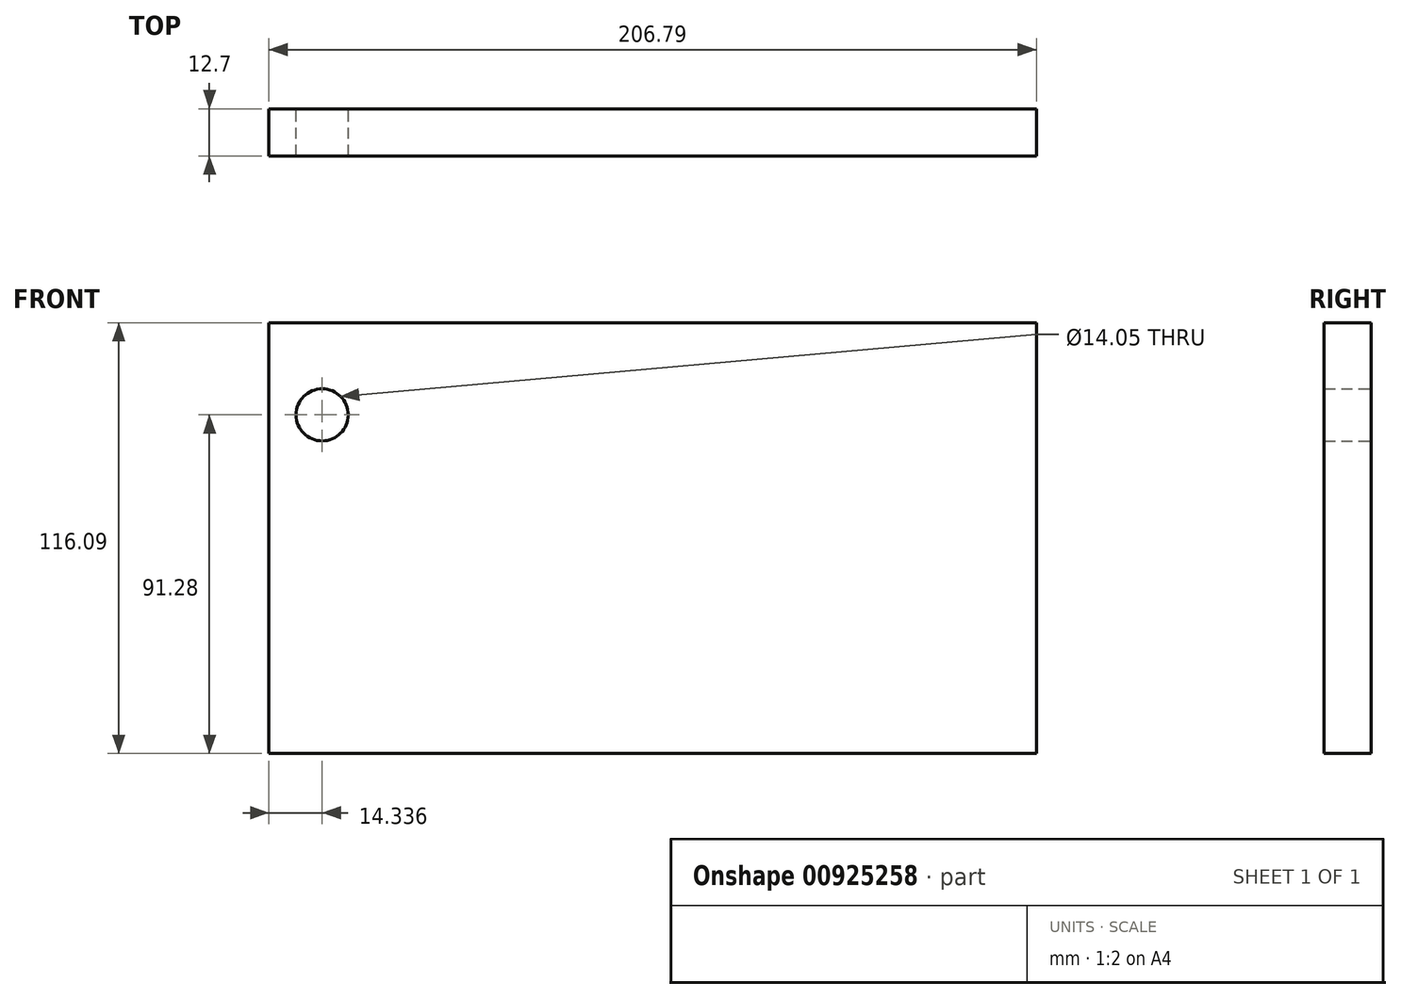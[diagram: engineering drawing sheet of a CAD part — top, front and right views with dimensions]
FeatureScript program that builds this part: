
annotation { "Feature Type Name" : "Feature", "Feature Type Description" : "" }
export const myFeature = defineFeature(function(context is Context, id is Id, definition is map)
    precondition{}
    {
        {
            var Q0;
            Q0=qCreatedBy(makeId("Front.planeOp"),FACE);
            var sketch = newSketch(context, id + "F0", { "sketchPlane" : qUnion([Q0])});
            skCircle(sketch, "E0", {"center": v(-88.93, 32.52) * mm, "radius": 7.02 * mm});
            skSolve(sketch);
        }
        {
            var Q0;
            Q0=qCreatedBy(makeId("Front.planeOp"),FACE);
            var sketch = newSketch(context, id + "F1", { "sketchPlane" : qUnion([Q0])});
            skLineSegment(sketch, "E1.bottom", {"start": v(-103.27, 57.33) * mm, "end": v(103.52, 57.33) * mm});
            skLineSegment(sketch, "E1.top", {"start": v(-103.27, -58.76) * mm, "end": v(103.52, -58.76) * mm});
            skLineSegment(sketch, "E1.left", {"start": v(-103.27, 57.33) * mm, "end": v(-103.27, -58.76) * mm});
            skLineSegment(sketch, "E1.right", {"start": v(103.52, 57.33) * mm, "end": v(103.52, -58.76) * mm});
            skLineSegment(sketch, "E2.bottom", {"start": v(103.52, -58.47) * mm, "end": v(98.4, -58.47) * mm});
            skLineSegment(sketch, "E2.top", {"start": v(103.52, -53.63) * mm, "end": v(98.4, -53.63) * mm});
            skLineSegment(sketch, "E2.left", {"start": v(103.52, -58.47) * mm, "end": v(103.52, -53.63) * mm});
            skLineSegment(sketch, "E2.right", {"start": v(98.4, -58.47) * mm, "end": v(98.4, -53.63) * mm});
            skSolve(sketch);
        }
        {
            var Q0;
            Q0 = qSketchRegion(id + "F1", true);
            extrude(context, id + "F2", {"entities" : qUnion([Q0]), "depth" : 12.7 * mm, "offsetDistance" : 25.4 * mm});
        }
        {
            var Q0;
            Q0 = qSketchRegion(id + "F0", true);
            extrude(context, id + "F3", {"entities" : qUnion([Q0]), "operationType" : NewBodyOperationType.REMOVE, "depth" : 25.4 * mm, "offsetDistance" : 25.4 * mm});
        }
    });
